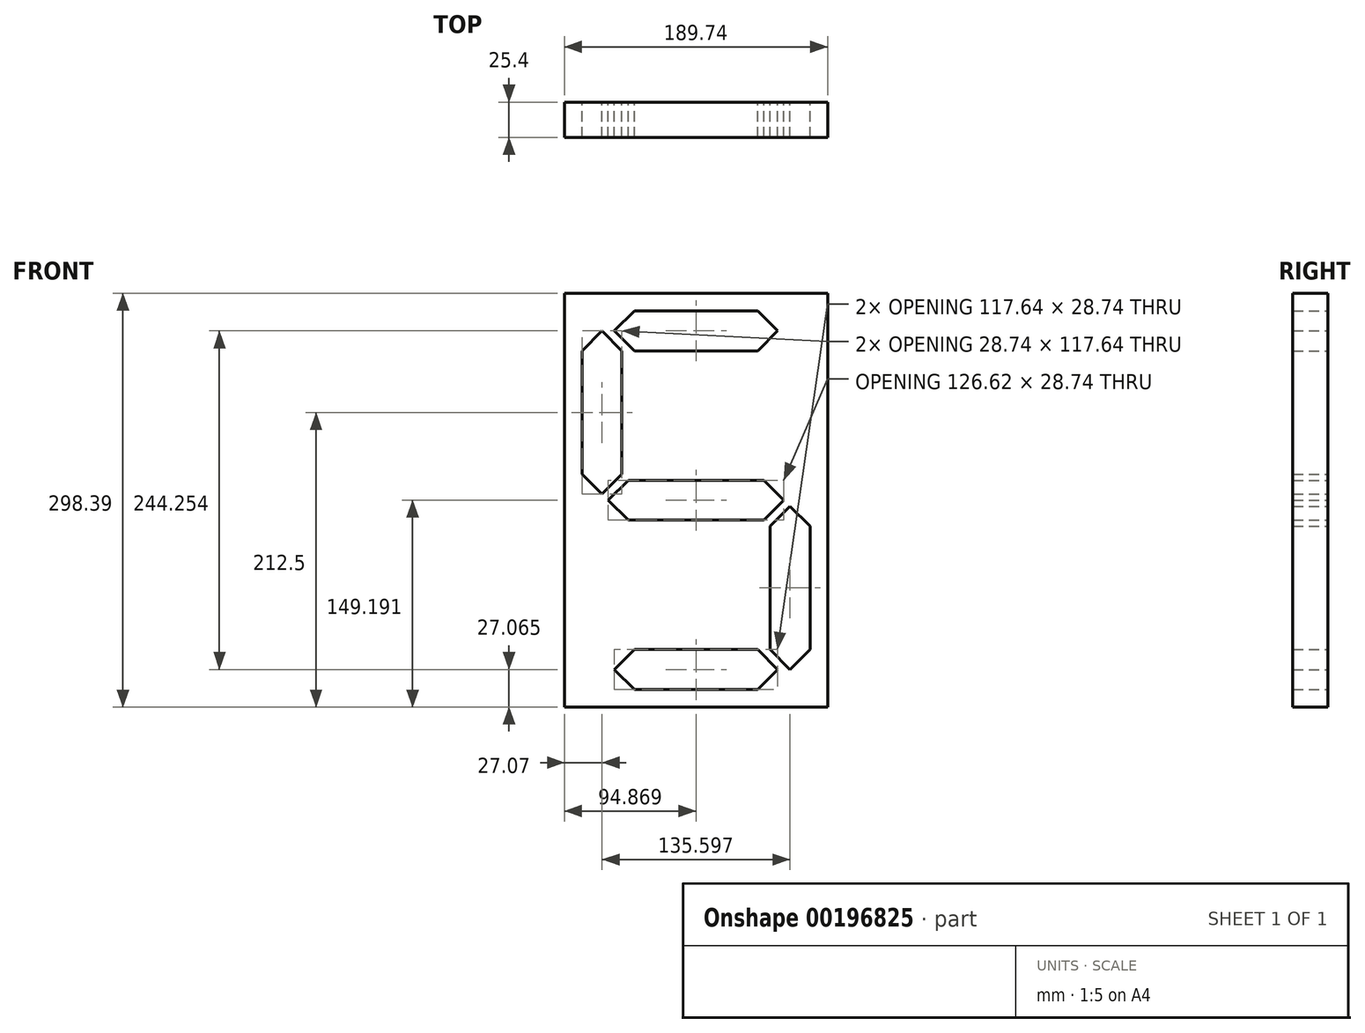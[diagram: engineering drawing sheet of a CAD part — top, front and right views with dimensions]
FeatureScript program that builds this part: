
annotation { "Feature Type Name" : "Feature", "Feature Type Description" : "" }
export const myFeature = defineFeature(function(context is Context, id is Id, definition is map)
    precondition{}
    {
        {
            var Q0;
            Q0=qCreatedBy(makeId("Front.planeOp"),FACE);
            var sketch = newSketch(context, id + "F0", { "sketchPlane" : qUnion([Q0])});
            skLineSegment(sketch, "E0.bottom", {"start": v(14.37, -44.45) * mm, "end": v(-14.37, -44.45) * mm});
            skLineSegment(sketch, "E0.top", {"start": v(14.37, 44.45) * mm, "end": v(-14.37, 44.45) * mm});
            skLineSegment(sketch, "E0.left", {"start": v(14.37, -44.45) * mm, "end": v(14.37, 44.45) * mm});
            skLineSegment(sketch, "E0.right", {"start": v(-14.37, -44.45) * mm, "end": v(-14.37, 44.45) * mm});
            skPoint(sketch, "E0.middle", {"position": v(0, 0) * mm});
            skLineSegment(sketch, "E1", {"start": v(-14.37, 44.45) * mm, "end": v(0, 58.82) * mm});
            skPoint(sketch, "E1.endSnap0", {"position": v(0, 44.45) * mm});
            skLineSegment(sketch, "E2", {"start": v(0, 58.82) * mm, "end": v(14.37, 44.45) * mm});
            skLineSegment(sketch, "E3", {"start": v(-14.37, -44.45) * mm, "end": v(0, -58.82) * mm});
            skPoint(sketch, "E3.endSnap0", {"position": v(0, -44.45) * mm});
            skLineSegment(sketch, "E4", {"start": v(0, -58.82) * mm, "end": v(14.37, -44.45) * mm});
            skLineSegment(sketch, "E5", {"start": v(8.98, 58.82) * mm, "end": v(23.35, 44.45) * mm});
            skLineSegment(sketch, "E6", {"start": v(0, 58.82) * mm, "end": v(8.98, 58.82) * mm});
            skLineSegment(sketch, "E7", {"start": v(8.98, 58.82) * mm, "end": v(23.35, 73.19) * mm});
            skLineSegment(sketch, "E8", {"start": v(23.35, 73.19) * mm, "end": v(112.25, 73.19) * mm});
            skLineSegment(sketch, "E9", {"start": v(112.25, 73.19) * mm, "end": v(126.62, 58.82) * mm});
            skLineSegment(sketch, "E10", {"start": v(126.62, 58.82) * mm, "end": v(112.25, 44.45) * mm});
            skLineSegment(sketch, "E11", {"start": v(121.23, 44.45) * mm, "end": v(135.6, 58.82) * mm});
            skLineSegment(sketch, "E12", {"start": v(135.6, 58.82) * mm, "end": v(126.62, 58.82) * mm});
            skLineSegment(sketch, "E13", {"start": v(23.35, 44.45) * mm, "end": v(112.25, 44.45) * mm});
            skLineSegment(sketch, "E14", {"start": v(135.6, 58.82) * mm, "end": v(149.97, 44.45) * mm});
            skLineSegment(sketch, "E15", {"start": v(149.97, 44.45) * mm, "end": v(149.97, -44.45) * mm});
            skLineSegment(sketch, "E16", {"start": v(149.97, -44.45) * mm, "end": v(135.6, -58.82) * mm});
            skLineSegment(sketch, "E17", {"start": v(135.6, -58.82) * mm, "end": v(121.23, -44.45) * mm});
            skLineSegment(sketch, "E18", {"start": v(121.23, -44.45) * mm, "end": v(121.23, 44.45) * mm});
            skLineSegment(sketch, "E19", {"start": v(135.6, -58.82) * mm, "end": v(135.6, -67.8) * mm});
            skLineSegment(sketch, "E20", {"start": v(0, -67.8) * mm, "end": v(0, -58.82) * mm});
            skLineSegment(sketch, "E21", {"start": v(135.6, -67.8) * mm, "end": v(149.97, -82.17) * mm});
            skLineSegment(sketch, "E22", {"start": v(149.97, -82.17) * mm, "end": v(149.97, -171.07) * mm});
            skLineSegment(sketch, "E23", {"start": v(149.97, -171.07) * mm, "end": v(135.6, -185.44) * mm});
            skLineSegment(sketch, "E24", {"start": v(135.6, -185.44) * mm, "end": v(121.23, -171.07) * mm});
            skLineSegment(sketch, "E25", {"start": v(121.23, -171.07) * mm, "end": v(121.23, -82.17) * mm});
            skLineSegment(sketch, "E26", {"start": v(121.23, -82.17) * mm, "end": v(135.6, -67.8) * mm});
            skLineSegment(sketch, "E27", {"start": v(135.6, -185.44) * mm, "end": v(126.62, -185.44) * mm});
            skLineSegment(sketch, "E28", {"start": v(126.62, -185.44) * mm, "end": v(112.25, -171.07) * mm});
            skLineSegment(sketch, "E29", {"start": v(126.62, -185.44) * mm, "end": v(112.25, -199.8) * mm});
            skLineSegment(sketch, "E30", {"start": v(112.25, -199.8) * mm, "end": v(23.35, -199.8) * mm});
            skLineSegment(sketch, "E31", {"start": v(23.35, -199.8) * mm, "end": v(8.98, -185.44) * mm});
            skLineSegment(sketch, "E32", {"start": v(8.98, -185.44) * mm, "end": v(23.35, -171.07) * mm});
            skLineSegment(sketch, "E33", {"start": v(23.35, -171.07) * mm, "end": v(112.25, -171.07) * mm});
            skLineSegment(sketch, "E34", {"start": v(0, -67.8) * mm, "end": v(14.37, -82.17) * mm});
            skLineSegment(sketch, "E35", {"start": v(14.37, -82.17) * mm, "end": v(14.37, -171.07) * mm});
            skLineSegment(sketch, "E36", {"start": v(14.37, -171.07) * mm, "end": v(0, -185.44) * mm});
            skLineSegment(sketch, "E37", {"start": v(0, -185.44) * mm, "end": v(-14.37, -171.07) * mm});
            skLineSegment(sketch, "E38", {"start": v(-14.37, -171.07) * mm, "end": v(-14.37, -82.17) * mm});
            skLineSegment(sketch, "E39", {"start": v(-14.37, -82.17) * mm, "end": v(0, -67.8) * mm});
            skLineSegment(sketch, "E40", {"start": v(8.98, -185.44) * mm, "end": v(0, -185.44) * mm});
            skLineSegment(sketch, "E41", {"start": v(4.5, -63.3) * mm, "end": v(18.86, -48.94) * mm});
            skLineSegment(sketch, "E42", {"start": v(18.86, -48.94) * mm, "end": v(116.74, -48.94) * mm});
            skLineSegment(sketch, "E43", {"start": v(116.74, -48.94) * mm, "end": v(131.1, -63.3) * mm});
            skLineSegment(sketch, "E44", {"start": v(131.1, -63.3) * mm, "end": v(116.74, -77.68) * mm});
            skLineSegment(sketch, "E45", {"start": v(116.74, -77.68) * mm, "end": v(18.86, -77.68) * mm});
            skLineSegment(sketch, "E46", {"start": v(18.86, -77.68) * mm, "end": v(4.5, -63.3) * mm});
            skLineSegment(sketch, "E47.bottom", {"start": v(-27.07, 85.89) * mm, "end": v(162.67, 85.89) * mm});
            skLineSegment(sketch, "E47.top", {"start": v(-27.07, -212.5) * mm, "end": v(162.67, -212.5) * mm});
            skLineSegment(sketch, "E47.left", {"start": v(-27.07, 85.89) * mm, "end": v(-27.07, -212.5) * mm});
            skLineSegment(sketch, "E47.right", {"start": v(162.67, 85.89) * mm, "end": v(162.67, -212.5) * mm});
            skPoint(sketch, "E48.end.orphan", {"position": v(135.6, -63.3) * mm});
            skLineSegment(sketch, "E49", {"start": v(131.1, -63.3) * mm, "end": v(135.6, -67.8) * mm});
            skPoint(sketch, "E50.end.orphan", {"position": v(0, -63.3) * mm});
            skLineSegment(sketch, "E51", {"start": v(4.5, -63.3) * mm, "end": v(0, -67.8) * mm});
            skSolve(sketch);
        }
        {
            var Q0;
            Q0=makeQuery(id+"F0.imprint","IMPRINT",FACE,{"disambiguationData":[TD([[makeQuery(id+"F0.imprint","IMPRINT",EDGE,{"derivedFrom":sQuery(id+"F0.wireOp",EDGE,"E0.right")}),1.0]])]});
            var Q1;
            Q1=makeQuery(id+"F0.imprint","IMPRINT",FACE,{"disambiguationData":[TD([[makeQuery(id+"F0.imprint","IMPRINT",EDGE,{"derivedFrom":sQuery(id+"F0.wireOp",EDGE,"E0.left")}),-1.0]])]});
            var Q2;
            Q2=makeQuery(id+"F0.imprint","IMPRINT",FACE,{"disambiguationData":[TD([[makeQuery(id+"F0.imprint","IMPRINT",EDGE,{"derivedFrom":sQuery(id+"F0.wireOp",EDGE,"E24")}),1.0]])]});
            var Q3;
            Q3=makeQuery(id+"F0.imprint","IMPRINT",FACE,{"disambiguationData":[TD([[makeQuery(id+"F0.imprint","IMPRINT",EDGE,{"derivedFrom":sQuery(id+"F0.wireOp",EDGE,"E11")}),-1.0]])]});
            var Q4;
            Q4=makeQuery(id+"F0.imprint","IMPRINT",FACE,{"disambiguationData":[TD([[makeQuery(id+"F0.imprint","IMPRINT",EDGE,{"derivedFrom":sQuery(id+"F0.wireOp",EDGE,"E34")}),-1.0]])]});
            extrude(context, id + "F1", {"entities" : qUnion([Q0, Q1, Q2, Q3, Q4]), "depth" : 25.4 * mm, "offsetDistance" : 25.4 * mm});
        }
    });
